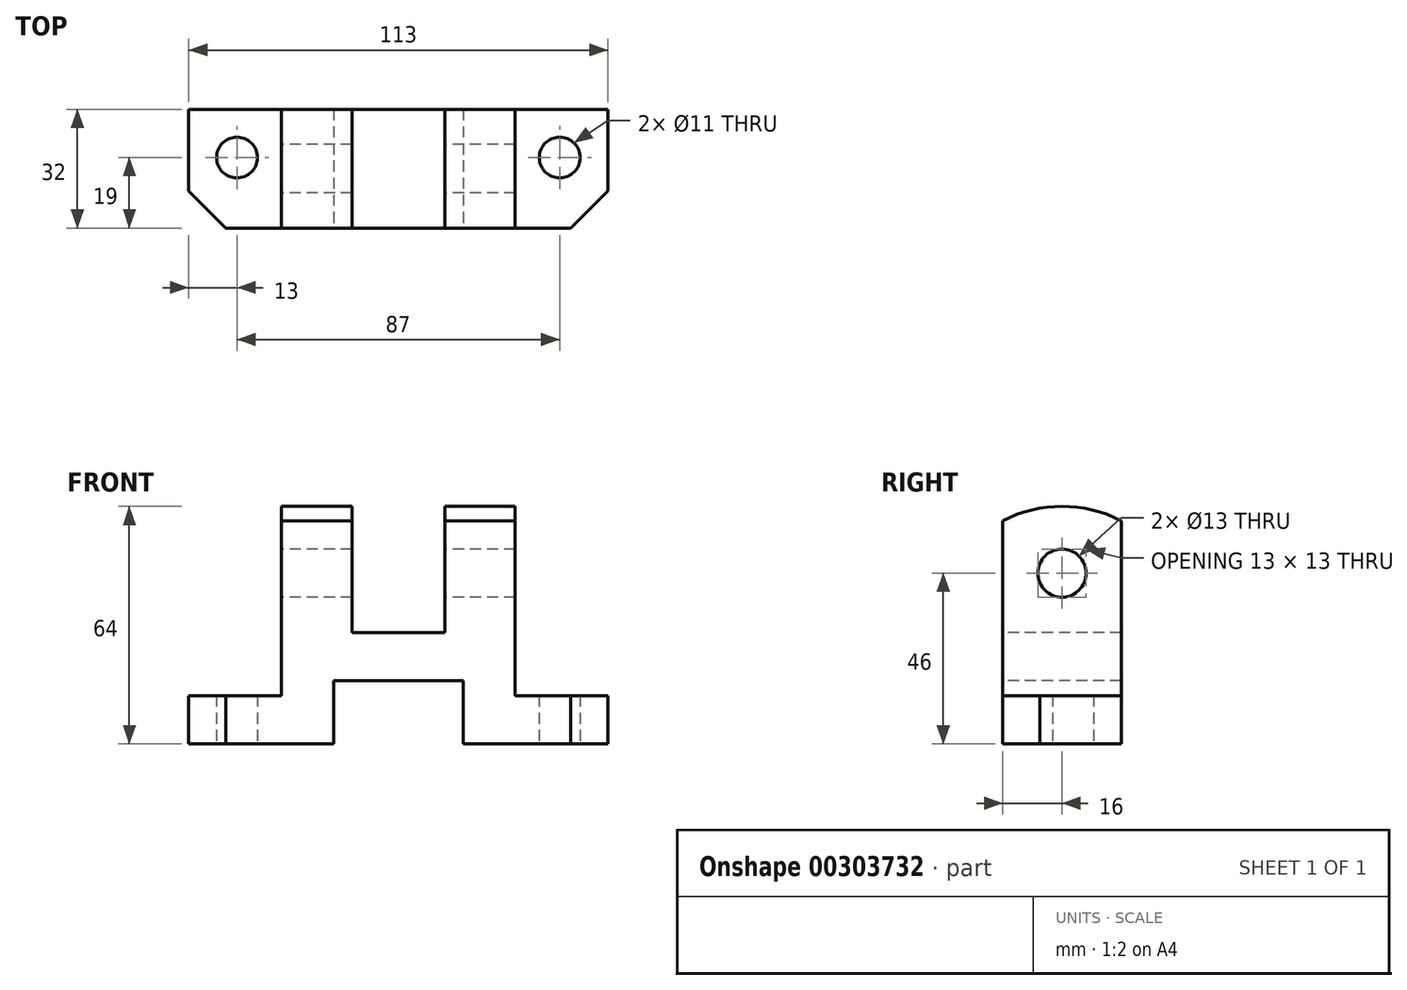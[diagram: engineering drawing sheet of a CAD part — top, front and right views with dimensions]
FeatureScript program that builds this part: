
annotation { "Feature Type Name" : "Feature", "Feature Type Description" : "" }
export const myFeature = defineFeature(function(context is Context, id is Id, definition is map)
    precondition{}
    {
        {
            var Q0;
            Q0=qCreatedBy(makeId("Front.planeOp"),FACE);
            var sketch = newSketch(context, id + "F0", { "sketchPlane" : qUnion([Q0])});
            skLineSegment(sketch, "E0", {"start": v(0, 0) * mm, "end": v(39, 0) * mm});
            skLineSegment(sketch, "E1", {"start": v(0, 0) * mm, "end": v(0, 13) * mm});
            skLineSegment(sketch, "E2", {"start": v(39, 0) * mm, "end": v(39, 17) * mm});
            skLineSegment(sketch, "E3", {"start": v(39, 17) * mm, "end": v(74, 17) * mm});
            skLineSegment(sketch, "E4", {"start": v(74, 17) * mm, "end": v(74, 0) * mm});
            skLineSegment(sketch, "E5", {"start": v(74, 0) * mm, "end": v(113, 0) * mm});
            skLineSegment(sketch, "E6", {"start": v(113, 0) * mm, "end": v(113, 13) * mm});
            skLineSegment(sketch, "E7", {"start": v(113, 13) * mm, "end": v(88, 13) * mm});
            skLineSegment(sketch, "E8", {"start": v(88, 13) * mm, "end": v(88, 46) * mm});
            skLineSegment(sketch, "E9", {"start": v(88, 13) * mm, "end": v(88, 64) * mm});
            skLineSegment(sketch, "E10", {"start": v(88, 64) * mm, "end": v(69, 64) * mm});
            skLineSegment(sketch, "E11", {"start": v(69, 64) * mm, "end": v(69, 30) * mm});
            skLineSegment(sketch, "E12", {"start": v(69, 30) * mm, "end": v(44, 30) * mm});
            skLineSegment(sketch, "E13", {"start": v(44, 30) * mm, "end": v(44, 64) * mm});
            skLineSegment(sketch, "E14", {"start": v(44, 64) * mm, "end": v(25, 64) * mm});
            skLineSegment(sketch, "E15", {"start": v(25, 64) * mm, "end": v(25, 13) * mm});
            skLineSegment(sketch, "E16", {"start": v(25, 13) * mm, "end": v(0, 13) * mm});
            skPoint(sketch, "E17.startSnap0", {"position": v(44, 47) * mm});
            skSolve(sketch);
        }
        {
            var Q0;
            Q0 = qSketchRegion(id + "F0", true);
            extrude(context, id + "F1", {"entities" : qUnion([Q0]), "oppositeDirection" : true, "depth" : 32 * mm});
        }
        {
            var Q0;
            Q0=qCreatedBy(makeId("Right.planeOp"),FACE);
            var sketch = newSketch(context, id + "F2", { "sketchPlane" : qUnion([Q0])});
            skArc(sketch, "E18", {"start": v(32, 60.13) * mm, "mid": v(16, 64) * mm, "end": v(0, 60.13) * mm});
            skCircle(sketch, "E19", {"center": v(16, 46) * mm, "radius": 6.5 * mm});
            skLineSegment(sketch, "E20", {"start": v(0, 46) * mm, "end": v(32.32, 46) * mm, "construction": true});
            skLineSegment(sketch, "E21", {"start": v(16, 64) * mm, "end": v(0, 64) * mm});
            skLineSegment(sketch, "E22", {"start": v(0, 64) * mm, "end": v(0, 60.13) * mm});
            skLineSegment(sketch, "E23", {"start": v(16, 64) * mm, "end": v(32, 64) * mm});
            skLineSegment(sketch, "E24", {"start": v(32, 64) * mm, "end": v(32, 60.13) * mm});
            skSolve(sketch);
        }
        {
            var Q0;
            Q0 = qSketchRegion(id + "F2", true);
            extrude(context, id + "F3", {"entities" : qUnion([Q0]), "operationType" : NewBodyOperationType.REMOVE, "endBound" : BoundingType.THROUGH_ALL, "depth" : 25 * mm});
        }
        {
            var Q0;
            Q0=qCreatedBy(makeId("Top.planeOp"),FACE);
            var sketch = newSketch(context, id + "F4", { "sketchPlane" : qUnion([Q0])});
            skLineSegment(sketch, "E25", {"start": v(0, 0) * mm, "end": v(10, 0) * mm});
            skLineSegment(sketch, "E26", {"start": v(113, 0) * mm, "end": v(103, 0) * mm});
            skLineSegment(sketch, "E27", {"start": v(10, 0) * mm, "end": v(0, 10) * mm});
            skLineSegment(sketch, "E28", {"start": v(103, 0) * mm, "end": v(113, 10) * mm});
            skCircle(sketch, "E29", {"center": v(100, 19) * mm, "radius": 5.5 * mm});
            skCircle(sketch, "E30", {"center": v(13, 19) * mm, "radius": 5.5 * mm});
            skLineSegment(sketch, "E31", {"start": v(113, 10) * mm, "end": v(113, 0) * mm});
            skLineSegment(sketch, "E32", {"start": v(0, 10) * mm, "end": v(0, 0) * mm});
            skSolve(sketch);
        }
        {
            var Q0;
            Q0 = qSketchRegion(id + "F4", true);
            extrude(context, id + "F5", {"entities" : qUnion([Q0]), "operationType" : NewBodyOperationType.REMOVE, "endBound" : BoundingType.THROUGH_ALL, "depth" : 25 * mm});
        }
    });
